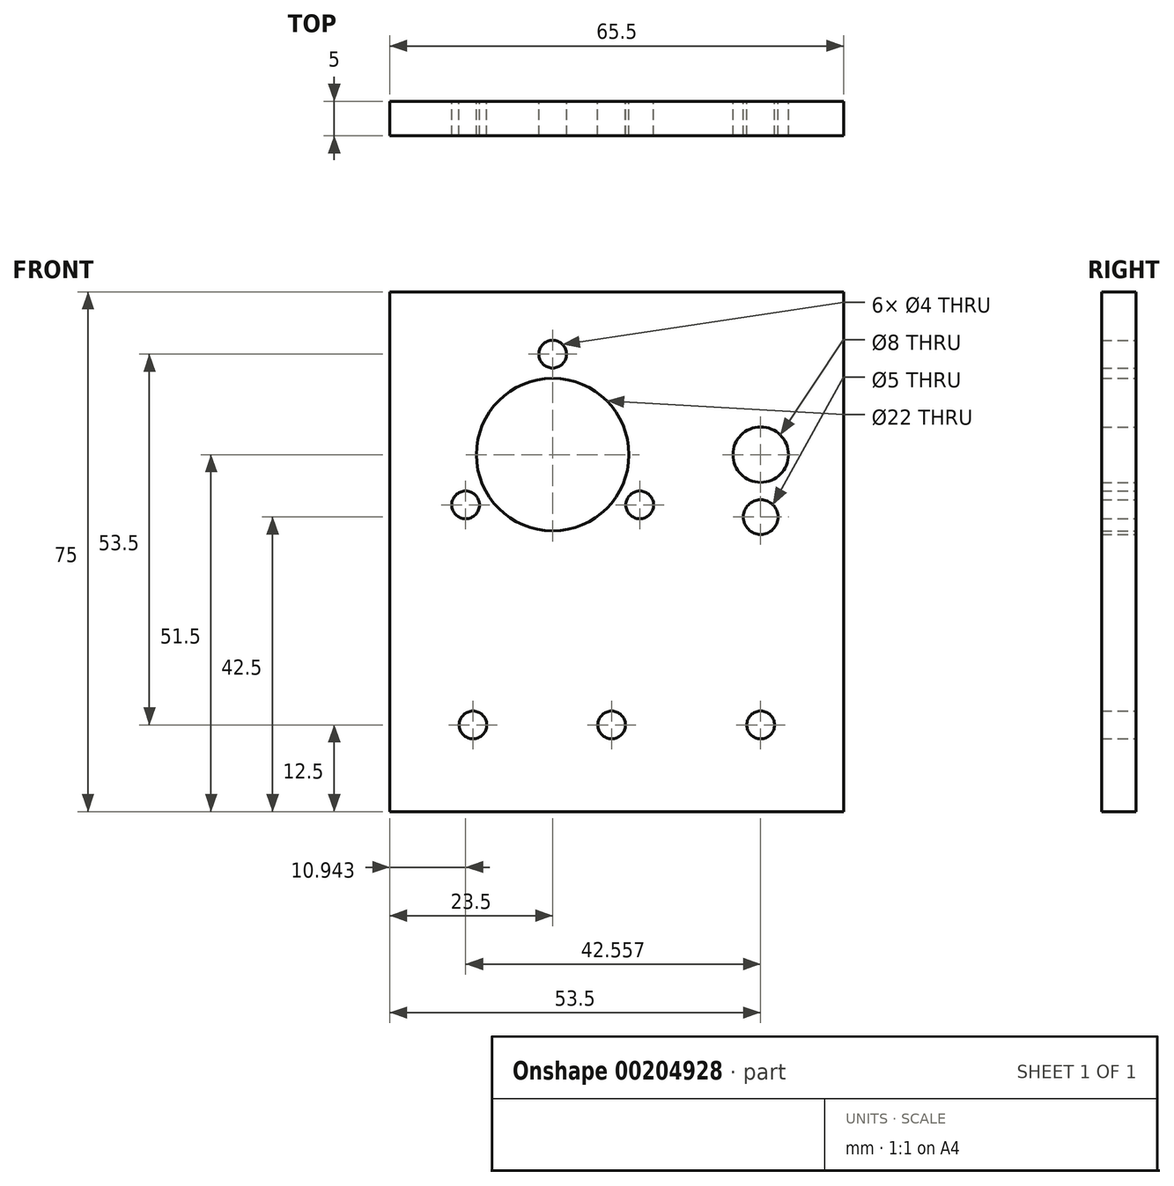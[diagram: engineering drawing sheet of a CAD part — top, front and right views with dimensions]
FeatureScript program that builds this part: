
annotation { "Feature Type Name" : "Feature", "Feature Type Description" : "" }
export const myFeature = defineFeature(function(context is Context, id is Id, definition is map)
    precondition{}
    {
        {
            var Q0;
            Q0=qCreatedBy(makeId("Front.planeOp"),FACE);
            var sketch = newSketch(context, id + "F0", { "sketchPlane" : qUnion([Q0])});
            skLineSegment(sketch, "E0.bottom", {"start": v(0, 25) * mm, "end": v(47, 25) * mm});
            skLineSegment(sketch, "E0.top", {"start": v(0, 75) * mm, "end": v(47, 75) * mm});
            skLineSegment(sketch, "E0.left", {"start": v(0, 25) * mm, "end": v(0, 75) * mm});
            skLineSegment(sketch, "E0.right", {"start": v(47, 25) * mm, "end": v(47, 75) * mm});
            skLineSegment(sketch, "E1.bottom", {"start": v(8, 36) * mm, "end": v(39, 36) * mm, "construction": true});
            skLineSegment(sketch, "E1.top", {"start": v(8, 67) * mm, "end": v(39, 67) * mm, "construction": true});
            skLineSegment(sketch, "E1.left", {"start": v(8, 36) * mm, "end": v(8, 67) * mm, "construction": true});
            skLineSegment(sketch, "E1.right", {"start": v(39, 36) * mm, "end": v(39, 67) * mm, "construction": true});
            skCircle(sketch, "E2", {"center": v(8, 67) * mm, "radius": 1.5 * mm, "construction": true});
            skCircle(sketch, "E3", {"center": v(39, 67) * mm, "radius": 1.5 * mm, "construction": true});
            skCircle(sketch, "E4", {"center": v(39, 36) * mm, "radius": 1.5 * mm, "construction": true});
            skCircle(sketch, "E5", {"center": v(8, 36) * mm, "radius": 1.5 * mm, "construction": true});
            skLineSegment(sketch, "E6", {"start": v(8, 36) * mm, "end": v(39, 67) * mm});
            skPoint(sketch, "E7", {"position": v(23.5, 51.5) * mm});
            skLineSegment(sketch, "E8", {"start": v(23.5, 51.5) * mm, "end": v(53.5, 51.5) * mm, "construction": true});
            skCircle(sketch, "E9", {"center": v(53.5, 51.5) * mm, "radius": 4 * mm});
            skCircle(sketch, "E10", {"center": v(53.5, 51.5) * mm, "radius": 12 * mm, "construction": true});
            skLineSegment(sketch, "E11.top", {"start": v(0, 0) * mm, "end": v(47, 0) * mm});
            skLineSegment(sketch, "E11.left", {"start": v(0, 25) * mm, "end": v(0, 0) * mm});
            skLineSegment(sketch, "E11.right", {"start": v(47, 25) * mm, "end": v(47, 0) * mm});
            skCircle(sketch, "E12", {"center": v(23.5, 51.5) * mm, "radius": 11 * mm});
            skLineSegment(sketch, "E13", {"start": v(53.5, 51.5) * mm, "end": v(53.5, 42.5) * mm});
            skCircle(sketch, "E14", {"center": v(53.5, 42.5) * mm, "radius": 2.5 * mm});
            skLineSegment(sketch, "E15", {"start": v(53.5, 51.5) * mm, "end": v(65.5, 51.5) * mm, "construction": true});
            skLineSegment(sketch, "E16", {"start": v(65.5, 51.5) * mm, "end": v(65.5, 0) * mm});
            skLineSegment(sketch, "E17", {"start": v(65.5, 0) * mm, "end": v(47, 0) * mm});
            skLineSegment(sketch, "E18", {"start": v(65.5, 51.5) * mm, "end": v(65.5, 75) * mm});
            skLineSegment(sketch, "E19", {"start": v(65.5, 75) * mm, "end": v(47, 75) * mm});
            skLineSegment(sketch, "E20", {"start": v(47, 12.5) * mm, "end": v(0, 12.5) * mm});
            skLineSegment(sketch, "E21", {"start": v(47, 12.5) * mm, "end": v(65.5, 12.5) * mm});
            skCircle(sketch, "E22", {"center": v(12, 12.5) * mm, "radius": 2 * mm});
            skCircle(sketch, "E23", {"center": v(32, 12.5) * mm, "radius": 2 * mm});
            skCircle(sketch, "E24", {"center": v(53.5, 12.5) * mm, "radius": 2 * mm});
            skLineSegment(sketch, "E25", {"start": v(23.5, 51.5) * mm, "end": v(23.5, 66) * mm});
            skCircle(sketch, "E26", {"center": v(23.5, 66) * mm, "radius": 2 * mm});
            skSolve(sketch);
        }
        {
            var Q0;
            Q0=makeQuery(id+"F0.imprint","IMPRINT",FACE,{"disambiguationData":[TD([[makeQuery(id+"F0.imprint","IMPRINT",EDGE,{"derivedFrom":sQuery(id+"F0.wireOp",EDGE,"E0.top")}),-1.0]])]});
            var Q1;
            {var subQ5=sQuery(id+"F0.wireOp",EDGE,"E0.right");Q1=makeQuery(id+"F0.imprint","IMPRINT",FACE,{"disambiguationData":[TD([[makeQuery(id+"F0.imprint","IMPRINT",EDGE,{"derivedFrom":subQ5}),-1.0]])]});}
            var Q2;
            {var subQ1=sQuery(id+"F0.wireOp",EDGE,"E0.bottom");Q2=makeQuery(id+"F0.imprint","IMPRINT",FACE,{"disambiguationData":[TD([[makeQuery(id+"F0.imprint","IMPRINT",EDGE,{"derivedFrom":subQ1}),-1.0]])]});}
            var Q3;
            {var subQ0=sQuery(id+"F0.wireOp",EDGE,"E17");Q3=makeQuery(id+"F0.imprint","IMPRINT",FACE,{"disambiguationData":[TD([[makeQuery(id+"F0.imprint","IMPRINT",EDGE,{"derivedFrom":subQ0}),-1.0]])]});}
            var Q4;
            {var subQ1=sQuery(id+"F0.wireOp",EDGE,"E11.top");Q4=makeQuery(id+"F0.imprint","IMPRINT",FACE,{"disambiguationData":[TD([[makeQuery(id+"F0.imprint","IMPRINT",EDGE,{"derivedFrom":subQ1}),1.0]])]});}
            extrude(context, id + "F1", {"entities" : qUnion([Q0, Q1, Q2, Q3, Q4]), "depth" : 5 * mm});
        }
        {
            var Q0;
            Q0=makeQuery(id+"F1.opExtrude","SWEPT_FACE",FACE,{"disambiguationData":[OSD([sQuery(id+"F0.wireOp",EDGE,"E26")])]});
            var Q1;
            Q1=makeQuery(id+"F1.opExtrude","SWEPT_FACE",FACE,{"disambiguationData":[OSD([sQuery(id+"F0.wireOp",EDGE,"E12")])]});
            circularPattern(context, id + "F2", {"patternType" : PatternType.FACE, "faces" : qUnion([Q0]), "axis" : qUnion([Q1]), "angle" : 360 * degree, "instanceCount" : 3, "equalSpace" : true});
        }
    });
